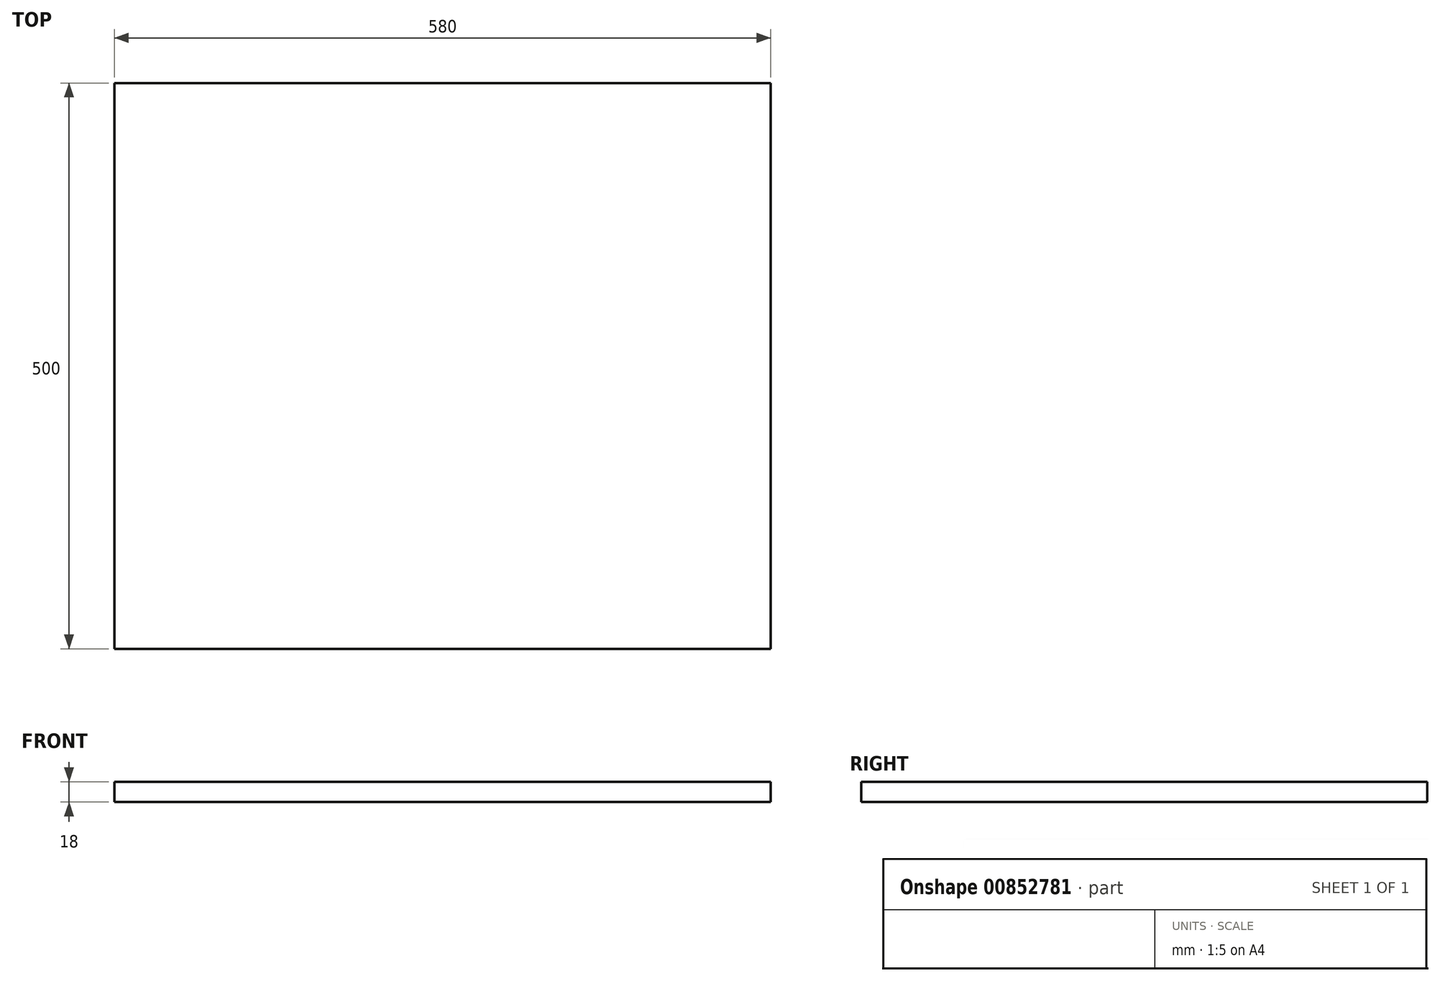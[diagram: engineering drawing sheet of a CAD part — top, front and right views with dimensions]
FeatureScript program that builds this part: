
annotation { "Feature Type Name" : "Feature", "Feature Type Description" : "" }
export const myFeature = defineFeature(function(context is Context, id is Id, definition is map)
    precondition{}
    {
        {
            var Q0;
            Q0=qCreatedBy(makeId("Top.planeOp"),FACE);
            var sketch = newSketch(context, id + "F0", { "sketchPlane" : qUnion([Q0])});
            skLineSegment(sketch, "E0.bottom", {"start": v(290, -250) * mm, "end": v(-290, -250) * mm});
            skLineSegment(sketch, "E0.top", {"start": v(290, 250) * mm, "end": v(-290, 250) * mm});
            skLineSegment(sketch, "E0.left", {"start": v(290, -250) * mm, "end": v(290, 250) * mm});
            skLineSegment(sketch, "E0.right", {"start": v(-290, -250) * mm, "end": v(-290, 250) * mm});
            skPoint(sketch, "E0.middle", {"position": v(0, 0) * mm});
            skSolve(sketch);
        }
        {
            var Q0;
            Q0=makeQuery(id+"F0.imprint","IMPRINT",FACE,{"disambiguationData":[TD([[makeQuery(id+"F0.imprint","IMPRINT",EDGE,{"derivedFrom":sQuery(id+"F0.wireOp",EDGE,"E0.bottom")}),-1.0]])]});
            extrude(context, id + "F1", {"entities" : qUnion([Q0]), "depth" : 18 * mm, "offsetDistance" : 25 * mm});
        }
    });
